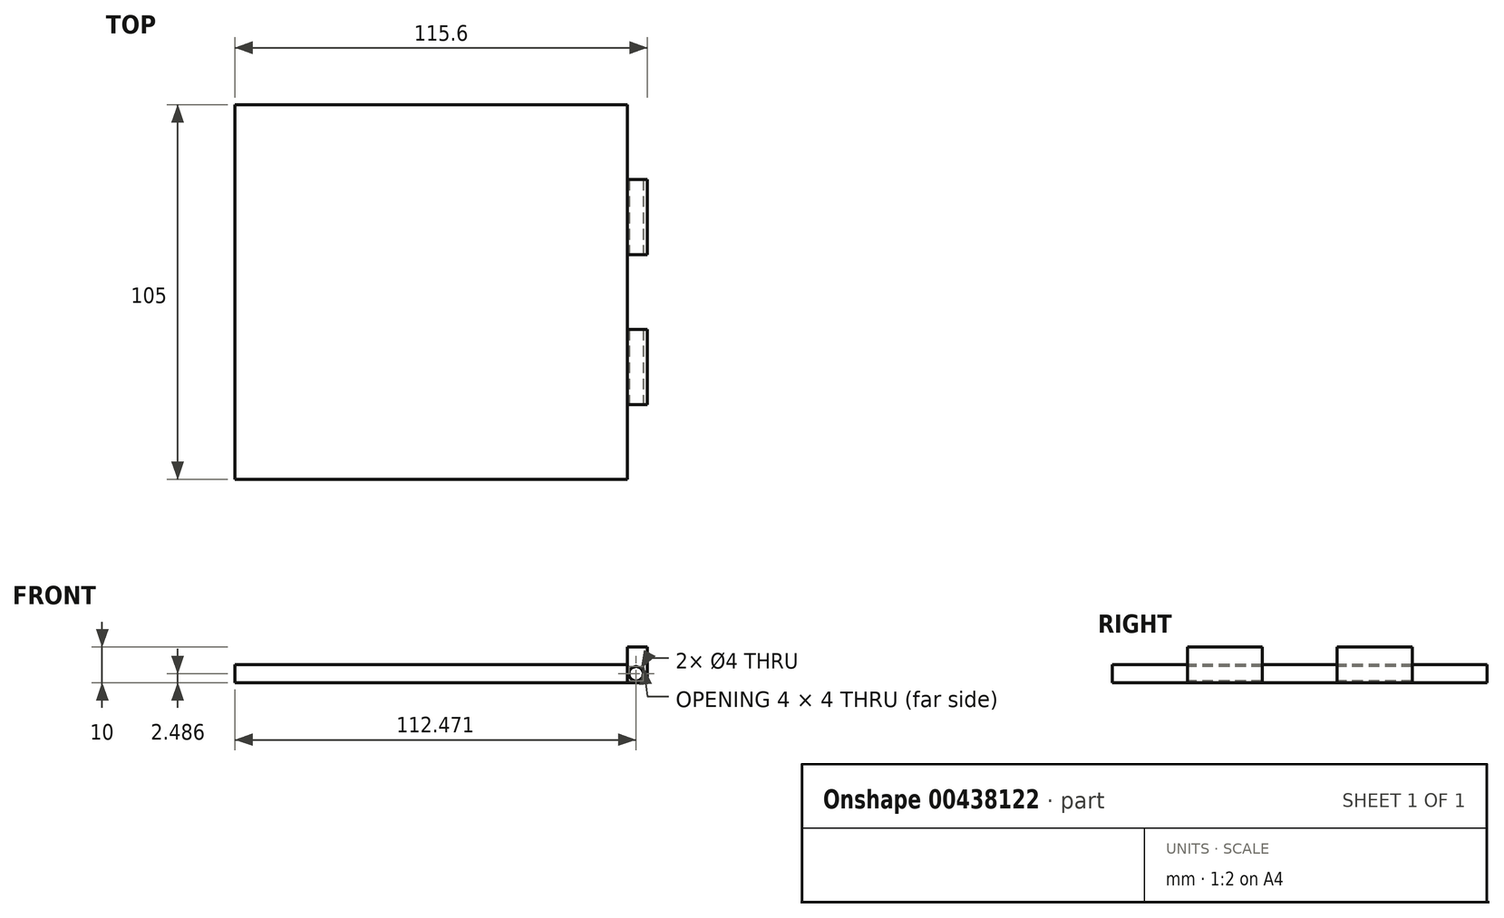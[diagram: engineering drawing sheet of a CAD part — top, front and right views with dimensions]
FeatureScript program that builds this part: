
annotation { "Feature Type Name" : "Feature", "Feature Type Description" : "" }
export const myFeature = defineFeature(function(context is Context, id is Id, definition is map)
    precondition{}
    {
        {
            var Q0;
            Q0=qCreatedBy(makeId("Top.planeOp"),FACE);
            var sketch = newSketch(context, id + "F0", { "sketchPlane" : qUnion([Q0])});
            skLineSegment(sketch, "E0.bottom", {"start": v(57.8, 52.5) * mm, "end": v(-57.8, 52.5) * mm});
            skLineSegment(sketch, "E0.top", {"start": v(57.8, -52.5) * mm, "end": v(-57.8, -52.5) * mm});
            skLineSegment(sketch, "E0.left", {"start": v(57.8, 31.5) * mm, "end": v(57.8, 10.5) * mm});
            skLineSegment(sketch, "E0.right", {"start": v(-57.8, 52.5) * mm, "end": v(-57.8, -52.5) * mm});
            skPoint(sketch, "E0.middle", {"position": v(0, 0) * mm});
            skPoint(sketch, "E1", {"position": v(52.2, 52.5) * mm});
            skLineSegment(sketch, "E2", {"start": v(52.2, 52.5) * mm, "end": v(52.2, 31.5) * mm});
            skLineSegment(sketch, "E3", {"start": v(52.2, 31.5) * mm, "end": v(57.8, 31.5) * mm});
            skLineSegment(sketch, "E4", {"start": v(57.8, 10.5) * mm, "end": v(52.2, 10.5) * mm});
            skLineSegment(sketch, "E5", {"start": v(52.2, 10.5) * mm, "end": v(52.2, -10.5) * mm});
            skLineSegment(sketch, "E6", {"start": v(52.2, -10.5) * mm, "end": v(57.8, -10.5) * mm});
            skLineSegment(sketch, "E7", {"start": v(57.8, -31.5) * mm, "end": v(52.2, -31.5) * mm});
            skLineSegment(sketch, "E8", {"start": v(52.2, -31.5) * mm, "end": v(52.2, -52.5) * mm});
            skLineSegment(sketch, "E9.trimOffspring", {"start": v(57.8, -10.5) * mm, "end": v(57.8, -31.5) * mm});
            skLineSegment(sketch, "E10", {"start": v(-69.43, 0) * mm, "end": v(68.1, 0) * mm, "construction": true});
            skSolve(sketch);
        }
        {
            var Q0;
            Q0=makeQuery(id+"F0.imprint","IMPRINT",FACE,{"disambiguationData":[TD([[makeQuery(id+"F0.imprint","IMPRINT",EDGE,{"derivedFrom":sQuery(id+"F0.wireOp",EDGE,"E0.left")}),-1.0]])]});
            extrude(context, id + "F1", {"entities" : qUnion([Q0]), "depth" : 5 * mm, "offsetDistance" : 25 * mm});
        }
        {
            var Q0;
            Q0=makeQuery(id+"F1.opExtrude","SWEPT_FACE",FACE,{"disambiguationData":[OSD([sQuery(id+"F0.wireOp",EDGE,"E7")])]});
            var sketch = newSketch(context, id + "F2", { "sketchPlane" : qUnion([Q0])});
            skCircle(sketch, "E11", {"center": v(54.67, 2.49) * mm, "radius": 1.75 * mm});
            skSolve(sketch);
        }
        {
            var Q0;
            Q0=sQuery(id+"F2.wireOp",VERTEX,"E11.center");
            var Q1;
            Q1=makeQuery(id+"F1.opExtrude","SWEPT_BODY",BODY,{"disambiguationData":[OSD([sQuery(id+"F0.wireOp",EDGE,"E0.bottom"),sQuery(id+"F0.wireOp",EDGE,"E0.top"),sQuery(id+"F0.wireOp",EDGE,"E0.left"),sQuery(id+"F0.wireOp",EDGE,"E0.right"),sQuery(id+"F0.wireOp",EDGE,"E2"),sQuery(id+"F0.wireOp",EDGE,"E3"),sQuery(id+"F0.wireOp",EDGE,"E4"),sQuery(id+"F0.wireOp",EDGE,"E5"),sQuery(id+"F0.wireOp",EDGE,"E6"),sQuery(id+"F0.wireOp",EDGE,"E7"),sQuery(id+"F0.wireOp",EDGE,"E8"),sQuery(id+"F0.wireOp",EDGE,"E9.trimOffspring")])]});
            hole(context, id + "F3", {"style" : HoleStyle.SIMPLE, "endStyle" : HoleEndStyle.THROUGH, "holeDiameter" : 4 * mm, "majorDiameter" : 5 * mm, "isTappedThrough" : true, "tappedDepth" : 12 * mm, "tapClearance" : 3, "locations" : qUnion([Q0]), "scope" : qUnion([Q1])});
        }
        {
            var Q0;
            Q0=makeQuery(id+"F1.opExtrude","CAP_FACE",FACE,{"disambiguationData":[OSD([sQuery(id+"F0.wireOp",EDGE,"E0.bottom"),sQuery(id+"F0.wireOp",EDGE,"E0.top"),sQuery(id+"F0.wireOp",EDGE,"E0.left"),sQuery(id+"F0.wireOp",EDGE,"E0.right"),sQuery(id+"F0.wireOp",EDGE,"E2"),sQuery(id+"F0.wireOp",EDGE,"E3"),sQuery(id+"F0.wireOp",EDGE,"E4"),sQuery(id+"F0.wireOp",EDGE,"E5"),sQuery(id+"F0.wireOp",EDGE,"E6"),sQuery(id+"F0.wireOp",EDGE,"E7"),sQuery(id+"F0.wireOp",EDGE,"E8"),sQuery(id+"F0.wireOp",EDGE,"E9.trimOffspring")])],"isStart":false});
            var sketch = newSketch(context, id + "F4", { "sketchPlane" : qUnion([Q0])});
            skLineSegment(sketch, "E12", {"start": v(52.2, 31.5) * mm, "end": v(52.2, 10.5) * mm});
            skLineSegment(sketch, "E13", {"start": v(52.2, -10.5) * mm, "end": v(52.2, -31.5) * mm});
            skSolve(sketch);
        }
        {
            var Q0;
            Q0=makeQuery(id+"F4.imprint","IMPRINT",FACE,{"disambiguationData":[TD([[makeQuery(id+"F4.imprint","IMPRINT",EDGE,{"derivedFrom":sQuery(id+"F4.wireOp",EDGE,"E12")}),1.0]])]});
            var Q1;
            Q1=makeQuery(id+"F4.imprint","IMPRINT",FACE,{"disambiguationData":[TD([[makeQuery(id+"F4.imprint","IMPRINT",EDGE,{"derivedFrom":sQuery(id+"F4.wireOp",EDGE,"E13")}),1.0]])]});
            extrude(context, id + "F5", {"entities" : qUnion([Q0, Q1]), "operationType" : NewBodyOperationType.ADD, "depth" : 5 * mm, "offsetDistance" : 25 * mm});
        }
    });
